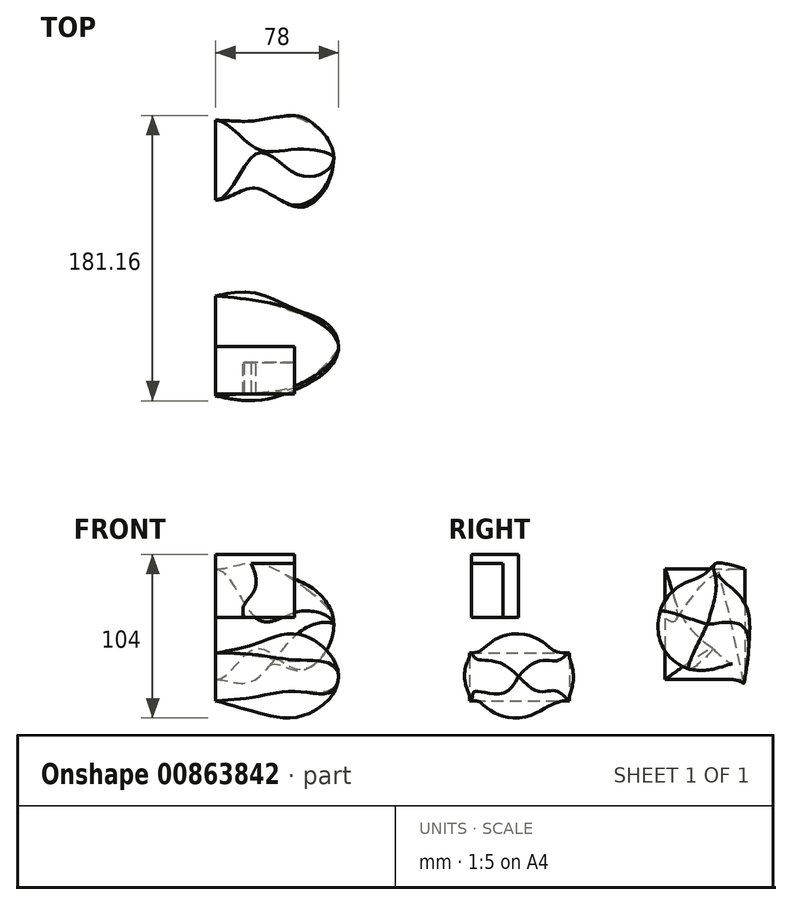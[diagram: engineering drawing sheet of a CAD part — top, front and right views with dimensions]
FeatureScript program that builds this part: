
annotation { "Feature Type Name" : "Feature", "Feature Type Description" : "" }
export const myFeature = defineFeature(function(context is Context, id is Id, definition is map)
    precondition{}
    {
        {
            var Q0;
            Q0=qCreatedBy(makeId("Front.planeOp"),FACE);
            var sketch = newSketch(context, id + "F0", { "sketchPlane" : qUnion([Q0])});
            skLineSegment(sketch, "E0.bottom", {"start": v(0, 0) * mm, "end": v(50, 0) * mm});
            skLineSegment(sketch, "E0.top", {"start": v(0, 40) * mm, "end": v(50, 40) * mm});
            skLineSegment(sketch, "E0.left", {"start": v(0, 0) * mm, "end": v(0, 40) * mm});
            skLineSegment(sketch, "E0.right", {"start": v(50, 0) * mm, "end": v(50, 40) * mm});
            skSolve(sketch);
        }
        {
            var Q0;
            Q0 = qSketchRegion(id + "F0", true);
            extrude(context, id + "F1", {"entities" : qUnion([Q0]), "depth" : 30 * mm, "offsetDistance" : 25 * mm});
        }
        {
            var Q0;
            Q0=makeQuery(id+"F1.opExtrude","CAP_FACE",FACE,{"disambiguationData":[OSD([sQuery(id+"F0.wireOp",EDGE,"E0.bottom"),sQuery(id+"F0.wireOp",EDGE,"E0.top"),sQuery(id+"F0.wireOp",EDGE,"E0.left"),sQuery(id+"F0.wireOp",EDGE,"E0.right")])],"isStart":false});
            var sketch = newSketch(context, id + "F2", { "sketchPlane" : qUnion([Q0])});
            skLineSegment(sketch, "E1", {"start": v(50, 34) * mm, "end": v(50, 0) * mm});
            skLineSegment(sketch, "E2", {"start": v(50, 0) * mm, "end": v(18, 0) * mm});
            skLineSegment(sketch, "E3", {"start": v(50, 34) * mm, "end": v(22.43, 34) * mm});
            skFitSpline(sketch, "E4", {"points": [v(22.43, 34) * mm, v(18, 0) * mm], "startDerivative": vector(32.97, -65.94) * mm, "endDerivative": vector(14.67, -40.1) * mm});
            skSolve(sketch);
        }
        {
            var Q0;
            Q0 = qSketchRegion(id + "F2", true);
            extrude(context, id + "F3", {"entities" : qUnion([Q0]), "oppositeDirection" : true, "depth" : 20 * mm, "offsetDistance" : 25 * mm});
        }
        {
            var Q0;
            Q0=makeQuery(id+"F3.opExtrude","SWEPT_BODY",BODY,{"disambiguationData":[OSD([sQuery(id+"F2.wireOp",EDGE,"E1"),sQuery(id+"F2.wireOp",EDGE,"E2"),sQuery(id+"F2.wireOp",EDGE,"E3"),sQuery(id+"F2.wireOp",EDGE,"E4")])]});
            var Q1;
            Q1=makeQuery(id+"F1.opExtrude","SWEPT_BODY",BODY,{"disambiguationData":[OSD([sQuery(id+"F0.wireOp",EDGE,"E0.bottom"),sQuery(id+"F0.wireOp",EDGE,"E0.top"),sQuery(id+"F0.wireOp",EDGE,"E0.left"),sQuery(id+"F0.wireOp",EDGE,"E0.right")])]});
            booleanBodies(context, id + "F4", {"operationType" : BooleanOperationType.SUBTRACTION, "tools" : qUnion([Q0]), "targets" : qUnion([Q1]), "keepTools" : true});
        }
        {
            var Q0;
            Q0=qCreatedBy(makeId("Right.planeOp"),FACE);
            cPlane(context, id + "F5", {"entities" : qUnion([Q0]), "cplaneType" : CPlaneType.OFFSET, "offset" : 25 * mm, "width" : 150 * mm, "height" : 150 * mm});
        }
        {
            var Q0;
            Q0=qCreatedBy(id+"F5.planeOp",FACE);
            cPlane(context, id + "F6", {"entities" : qUnion([Q0]), "cplaneType" : CPlaneType.OFFSET, "offset" : 25 * mm, "width" : 150 * mm, "height" : 150 * mm});
        }
        {
            var Q0;
            Q0=qCreatedBy(id+"F6.planeOp",FACE);
            cPlane(context, id + "F7", {"entities" : qUnion([Q0]), "cplaneType" : CPlaneType.OFFSET, "offset" : 25 * mm, "width" : 150 * mm, "height" : 150 * mm});
        }
        {
            var Q0;
            Q0=qCreatedBy(id+"F7.planeOp",FACE);
            cPlane(context, id + "F8", {"entities" : qUnion([Q0]), "cplaneType" : CPlaneType.OFFSET, "offset" : 3 * mm, "width" : 150 * mm, "height" : 150 * mm});
        }
        {
            var Q0;
            Q0=qCreatedBy(makeId("Right.planeOp"),FACE);
            var sketch = newSketch(context, id + "F9", { "sketchPlane" : qUnion([Q0]) });
            skLineSegment(sketch, "E5.bottom", {"start": v(-31.24, -22.72) * mm, "end": v(32.33, -22.72) * mm});
            skLineSegment(sketch, "E5.top", {"start": v(-31.24, -53.1) * mm, "end": v(32.33, -53.1) * mm});
            skLineSegment(sketch, "E5.left", {"start": v(-31.24, -22.72) * mm, "end": v(-31.24, -53.1) * mm});
            skLineSegment(sketch, "E5.right", {"start": v(32.33, -22.72) * mm, "end": v(32.33, -53.1) * mm});
            skSolve(sketch);
        }
        {
            var Q0;
            Q0=qCreatedBy(id+"F5.planeOp",FACE);
            var sketch = newSketch(context, id + "F10", { "sketchPlane" : qUnion([Q0]) });
            skArc(sketch, "E6", {"start": v(29.46, -24.46) * mm, "mid": v(0.21, -16.99) * mm, "end": v(-29.2, -23.76) * mm});
            skArc(sketch, "E7", {"start": v(-29.2, -50.64) * mm, "mid": v(0.13, -60.18) * mm, "end": v(29.46, -50.64) * mm});
            skArc(sketch, "E8", {"start": v(-29.2, -23.76) * mm, "mid": v(-34.24, -37.2) * mm, "end": v(-29.2, -50.64) * mm});
            skArc(sketch, "E9", {"start": v(29.46, -50.64) * mm, "mid": v(34.22, -37.55) * mm, "end": v(29.46, -24.46) * mm});
            skSolve(sketch);
        }
        {
            var Q0;
            Q0=qCreatedBy(id+"F6.planeOp",FACE);
            var sketch = newSketch(context, id + "F11", { "sketchPlane" : qUnion([Q0]) });
            skArc(sketch, "E10", {"start": v(23.2, -27.78) * mm, "mid": v(-0.62, -10.52) * mm, "end": v(-24.98, -27.03) * mm});
            skArc(sketch, "E11", {"start": v(-25.92, -46.98) * mm, "mid": v(-1.79, -63.7) * mm, "end": v(22.08, -46.6) * mm});
            skArc(sketch, "E12", {"start": v(22.08, -46.6) * mm, "mid": v(24, -37.28) * mm, "end": v(23.2, -27.78) * mm});
            skArc(sketch, "E13", {"start": v(-24.98, -27.03) * mm, "mid": v(-27.59, -36.9) * mm, "end": v(-25.92, -46.98) * mm});
            skSolve(sketch);
        }
        {
            var Q0;
            Q0=qCreatedBy(id+"F7.planeOp",FACE);
            var sketch = newSketch(context, id + "F12", { "sketchPlane" : qUnion([Q0]) });
            skArc(sketch, "E14", {"start": v(7.37, -30.56) * mm, "mid": v(-0.28, -27.3) * mm, "end": v(-7.64, -31.17) * mm});
            skArc(sketch, "E15", {"start": v(7.37, -30.56) * mm, "mid": v(10.01, -37.54) * mm, "end": v(7.37, -44.5) * mm});
            skArc(sketch, "E16", {"start": v(7.37, -44.5) * mm, "mid": v(1.16, -47.69) * mm, "end": v(-5.56, -45.81) * mm});
            skArc(sketch, "E17", {"start": v(-5.56, -45.81) * mm, "mid": v(-9.63, -38.92) * mm, "end": v(-7.64, -31.17) * mm});
            skSolve(sketch);
        }
        {
            var Q0;
            Q0=qCreatedBy(id+"F8.planeOp",FACE);
            var sketch = newSketch(context, id + "F13", { "sketchPlane" : qUnion([Q0]) });
            skPoint(sketch, "E18", {"position": v(0, -37.44) * mm});
            skSolve(sketch);
        }
        {
            var Q0;
            Q0=makeQuery(id+"F9.imprint","IMPRINT",FACE,{"disambiguationData":[TD([[makeQuery(id+"F9.imprint","IMPRINT",EDGE,{"derivedFrom":sQuery(id+"F9.wireOp",EDGE,"E5.bottom")}),-1.0]])]});
            var Q1;
            Q1=makeQuery(id+"F10.imprint","IMPRINT",FACE,{"disambiguationData":[TD([[makeQuery(id+"F10.imprint","IMPRINT",EDGE,{"derivedFrom":sQuery(id+"F10.wireOp",EDGE,"E6")}),1.0]])]});
            var Q2;
            Q2=makeQuery(id+"F11.imprint","IMPRINT",FACE,{"disambiguationData":[TD([[makeQuery(id+"F11.imprint","IMPRINT",EDGE,{"derivedFrom":sQuery(id+"F11.wireOp",EDGE,"E10")}),1.0]])]});
            var Q3;
            Q3=makeQuery(id+"F12.imprint","IMPRINT",FACE,{"disambiguationData":[TD([[makeQuery(id+"F12.imprint","IMPRINT",EDGE,{"derivedFrom":sQuery(id+"F12.wireOp",EDGE,"E14")}),1.0]])]});
            var Q4;
            Q4=sQuery(id+"F13.wireOp",VERTEX,"E18");
            loft(context, id + "F14", {"sheetProfilesArray" : [{ "sheetProfileEntities" : qUnion([Q0]) }, { "sheetProfileEntities" : qUnion([Q1]) }, { "sheetProfileEntities" : qUnion([Q2]) }, { "sheetProfileEntities" : qUnion([Q3]) }, { "sheetProfileEntities" : qUnion([Q4]) }], "endCondition" : LoftEndDerivativeType.TANGENT_TO_PROFILE, "endMagnitude" : 1});
        }
        {
            var Q0;
            Q0=qCreatedBy(makeId("Right.planeOp"),FACE);
            var sketch = newSketch(context, id + "F15", { "sketchPlane" : qUnion([Q0]) });
            skLineSegment(sketch, "E19.bottom", {"start": v(93.16, 30.56) * mm, "end": v(143.84, 30.56) * mm});
            skLineSegment(sketch, "E19.top", {"start": v(93.16, -39.5) * mm, "end": v(143.84, -39.5) * mm});
            skLineSegment(sketch, "E19.left", {"start": v(93.16, 30.56) * mm, "end": v(93.16, -39.5) * mm});
            skLineSegment(sketch, "E19.right", {"start": v(143.84, 30.56) * mm, "end": v(143.84, -39.5) * mm});
            skSolve(sketch);
        }
        {
            var Q0;
            Q0=qCreatedBy(id+"F5.planeOp",FACE);
            var sketch = newSketch(context, id + "F16", { "sketchPlane" : qUnion([Q0]) });
            skLineSegment(sketch, "E20", {"start": v(126.35, 34.49) * mm, "end": v(100.67, 0) * mm});
            skLineSegment(sketch, "E21", {"start": v(100.67, 0) * mm, "end": v(143.53, -39.7) * mm});
            skLineSegment(sketch, "E22", {"start": v(143.53, -39.7) * mm, "end": v(126.35, 34.49) * mm});
            skSolve(sketch);
        }
        {
            var Q0;
            Q0=qCreatedBy(id+"F6.planeOp",FACE);
            var sketch = newSketch(context, id + "F17", { "sketchPlane" : qUnion([Q0]) });
            skCircle(sketch, "E23", {"center": v(117.87, -4.63) * mm, "radius": 28.9 * mm});
            skSolve(sketch);
        }
        {
            var Q0;
            Q0=qCreatedBy(id+"F7.planeOp",FACE);
            var sketch = newSketch(context, id + "F18", { "sketchPlane" : qUnion([Q0]) });
            skPoint(sketch, "E24", {"position": v(119.96, -4.7) * mm});
            skSolve(sketch);
        }
        {
            var Q0;
            Q0 = qSketchRegion(id + "F15", true);
            var Q1;
            Q1 = qSketchRegion(id + "F16", true);
            var Q2;
            Q2 = qSketchRegion(id + "F17", true);
            var Q3;
            Q3=sQuery(id+"F18.wireOp",VERTEX,"E24");
            loft(context, id + "F19", {"sheetProfilesArray" : [{ "sheetProfileEntities" : qUnion([Q0]) }, { "sheetProfileEntities" : qUnion([Q1]) }, { "sheetProfileEntities" : qUnion([Q2]) }, { "sheetProfileEntities" : qUnion([Q3]) }], "startCondition" : LoftEndDerivativeType.NORMAL_TO_PROFILE, "startMagnitude" : 1, "endCondition" : LoftEndDerivativeType.TANGENT_TO_PROFILE, "endMagnitude" : 1});
        }
    });
